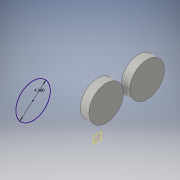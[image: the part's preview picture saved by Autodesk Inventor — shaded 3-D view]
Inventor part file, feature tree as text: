
AUTODESK INVENTOR PART (.ipt)
format: ipt  version: 2016 (Build 200138000, 138)  size: 99,328 bytes
history: native  units: in
note: dims shown in document units (in); Inventor stores cm internally (conversion verified against a paired STEP export)
features: sketch x2, plane x1, extrude x1
ambient origin geometry x8: Origin, YZ Plane, XZ Plane, XY Plane, X Axis, Y Axis, Z Axis, Center Point
bodies: Body1 (feature_tree)
feature tree (4):
  sketch  "Sketch7"  dims[d15=4.0in d18=4.0in]
  plane  "Work Plane1"
  extrude  "Extrusion3"  Depth=4.0in
  sketch  "Sketch8"  dims[d19=4.0in d20=4.75in d21=4.0in d22=1.0in d23=0.0in]
